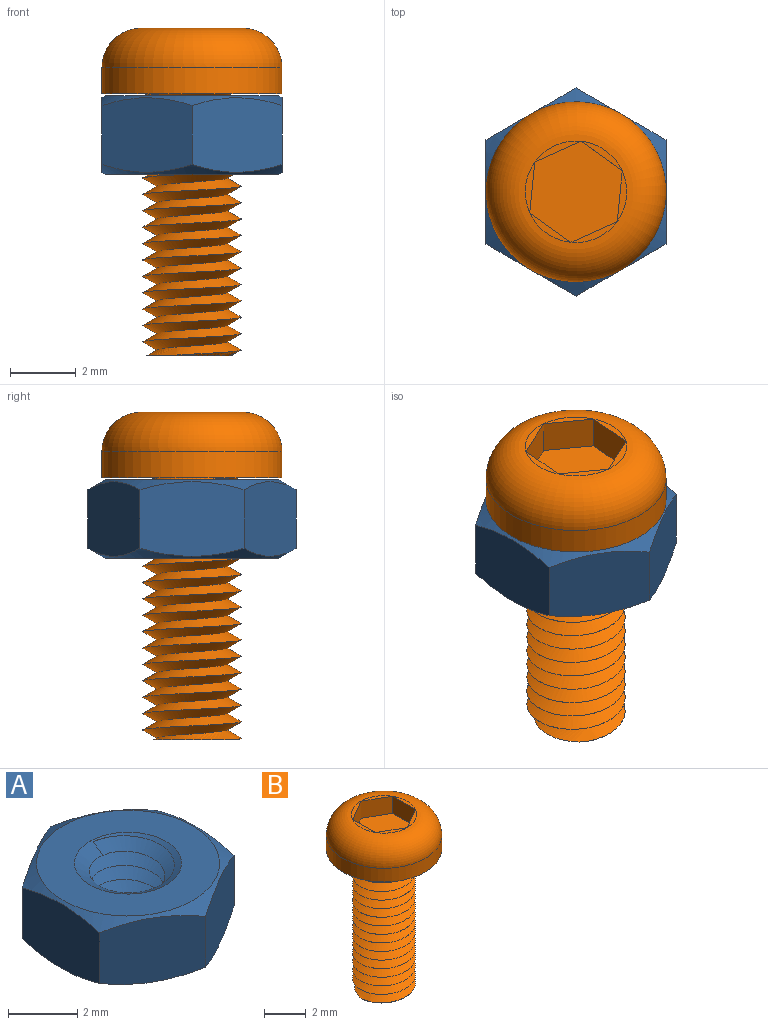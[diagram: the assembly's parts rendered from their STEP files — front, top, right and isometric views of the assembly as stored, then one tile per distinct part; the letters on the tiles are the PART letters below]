
ASSEMBLY  parts=2 mates=1
PART A: 15 faces, bbox 6.4x6.4x2.9 mm
  f0: cone r=0mm half-angle=60deg, axis (0,0,1), area 2.7mm2, adj f2,f12,f13,f14
  f1: cone r=0mm half-angle=60deg, axis (0,0,-1), area 2.7mm2, adj f11,f12,f13,f14
  f2: plane 5.3x5.3mm, normal (0,0,1), area 14.5mm2, adj f0,f3
  f3: cone r=2.65mm half-angle=60deg, axis (0,0,-1), area 4.8mm2, adj f2,f4,f5,f6,f7,f8,f9
  f4: plane 2.75x2.29mm, normal (0.5,0.87,0), area 6.7mm2, adj f3,f5,f9,f10
  f5: plane 3.18x2.29mm, normal (1,0,0), area 6.7mm2, adj f3,f4,f6,f10
  f6: plane 2.75x2.29mm, normal (0.5,-0.87,0), area 6.7mm2, adj f3,f5,f7,f10
  f7: plane 2.75x2.29mm, normal (-0.5,-0.87,0), area 6.7mm2, adj f3,f6,f8,f10
  f8: plane 3.18x2.29mm, normal (-1,0,0), area 6.7mm2, adj f3,f7,f9,f10
  f9: plane 2.75x2.29mm, normal (-0.5,0.87,0), area 6.7mm2, adj f3,f4,f8,f10
  f10: cone r=2.65mm half-angle=60deg, axis (0,0,1), area 4.8mm2, adj f4,f5,f6,f7,f8,f9,f11
  f11: plane 5.3x5.3mm, normal (0,0,-1), area 14.5mm2, adj f1,f10
  f12: cylinder r=1.5mm len=3mm, axis (0,0,-1), area 0mm2, adj f0,f1,f13,f14
  f13: bspline ~3.46x3mm, area 17mm2, adj f0,f1,f12,f14
  f14: bspline ~3.46x3mm, area 17mm2, adj f0,f1,f12,f13
PART B: 20 faces, bbox 6.3x6.3x10.7 mm
  f0: plane 1.55x0.21mm, normal (0,0,1), area 0.2mm2, adj f12,f13
  f1: plane 1.35x0.77mm, normal (0,0,1), area 0.2mm2, adj f12,f14
  f2: plane 1.34x0.78mm, normal (0,0,1), area 0.2mm2, adj f12,f15
  f3: plane 1.55x0.21mm, normal (0,0,1), area 0.2mm2, adj f12,f16
  f4: plane 1.35x0.77mm, normal (0,0,1), area 0.2mm2, adj f12,f17
  f5: cylinder r=1.5mm len=8mm, axis (0,0,-1), area 0.1mm2, adj f6,f7,f8,f9
  f6: plane 2.93x2.92mm, normal (0,0,-1), area 5.2mm2, adj f5,f7,f8
  f7: bspline ~8.5x3.46mm, area 64.8mm2, adj f5,f6,f8,f9
  f8: bspline ~8.58x3.46mm, area 64.8mm2, adj f5,f6,f7,f9
  f9: plane 5.85x5.85mm, normal (0,0,-1), area 18.5mm2, adj f5,f7,f8,f10
  f10: cylinder r=2.75mm len=5.5mm, axis (0,0,-1), area 13.8mm2, adj f9,f12
  f11: plane 1.34x0.78mm, normal (0,0,1), area 0.2mm2, adj f12,f18
  f12: torus R=1.55mm, axis (0,0,1), area 27.4mm2, adj f0,f1,f2,f3,f4,f10,f11
  f13: plane 1.55x1mm, normal (-1,-0.01,0), area 1.5mm2, adj f0,f14,f18,f19
  f14: plane 1.35x1mm, normal (-0.49,-0.87,0), area 1.6mm2, adj f1,f13,f15,f19
  f15: plane 1.34x1mm, normal (0.51,-0.86,0), area 1.5mm2, adj f2,f14,f16,f19
  f16: plane 1.55x1mm, normal (1,0.01,0), area 1.5mm2, adj f3,f15,f17,f19
  f17: plane 1.35x1mm, normal (0.49,0.87,0), area 1.6mm2, adj f4,f16,f18,f19
  f18: plane 1.34x1mm, normal (-0.51,0.86,0), area 1.5mm2, adj f11,f13,f17,f19
  f19: plane 3.1x2.69mm, normal (0,0,1), area 6.2mm2, adj f13,f14,f15,f16,f17,f18
PLACE A at identity fixed
PLACE B rot(axis=(0,0,1),54deg) t=(0,0,-5.54)mm
MATE cylindrical A.f12 <-> B.f5  axis (0,0,1) through (0,0,0)mm
